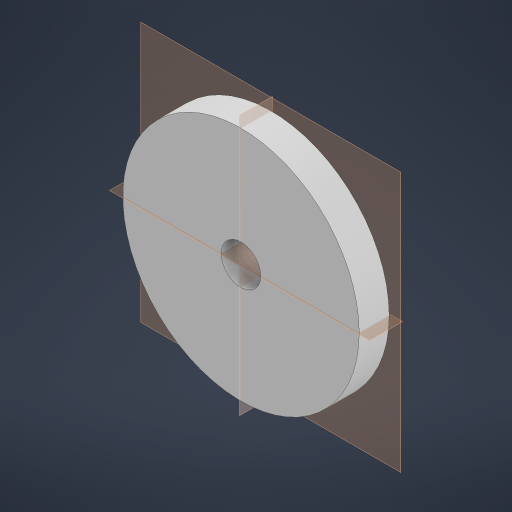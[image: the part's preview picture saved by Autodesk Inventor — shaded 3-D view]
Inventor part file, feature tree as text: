
AUTODESK INVENTOR PART (.ipt)
format: ipt  version: 2024.1 (Build 281209000, 209)  size: 169,472 bytes
history: native  units: in
note: dims shown in document units (in); Inventor stores cm internally (conversion verified against a paired STEP export)
features: extrude x1, sketch x1
ambient origin geometry x8: Origin, YZ Plane, XZ Plane, XY Plane, X Axis, Y Axis, Z Axis, Center Point
bodies: Solid1 (feature_tree)
feature tree (2):
  extrude  "Extrusion1"  Depth=0.38in
  sketch  "Sketch1"  dims[d0=3.0in d1=0.5in d2=0.38in d3=0.0in]
